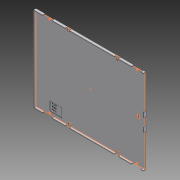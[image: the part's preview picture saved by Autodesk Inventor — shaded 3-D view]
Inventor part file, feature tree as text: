
AUTODESK INVENTOR PART (.ipt)
format: ipt  version: 2011 (Build 150239000, 239)  size: 273,920 bytes
history: native  units: in
note: dims shown in document units (in); Inventor stores cm internally (conversion verified against a paired STEP export)
features: sketch x4, other x1, imported_body x1, extrude x1
ambient origin geometry x8: Origin, YZ Plane, XZ Plane, XY Plane, X Axis, Y Axis, Z Axis, Center Point
feature tree (7):
  other  "Case Bottom"
  imported_body  "Base1"
  sketch  "Sketch1"  dims[d0=0.7874in d1=0.5906in]
  sketch  "Sketch2"  dims[d2=0.0197in d3=0.0in]
  sketch  "Sketch3"
  extrude  "Extrusion1"  Depth=0.5906in
  sketch  "Sketch4"
